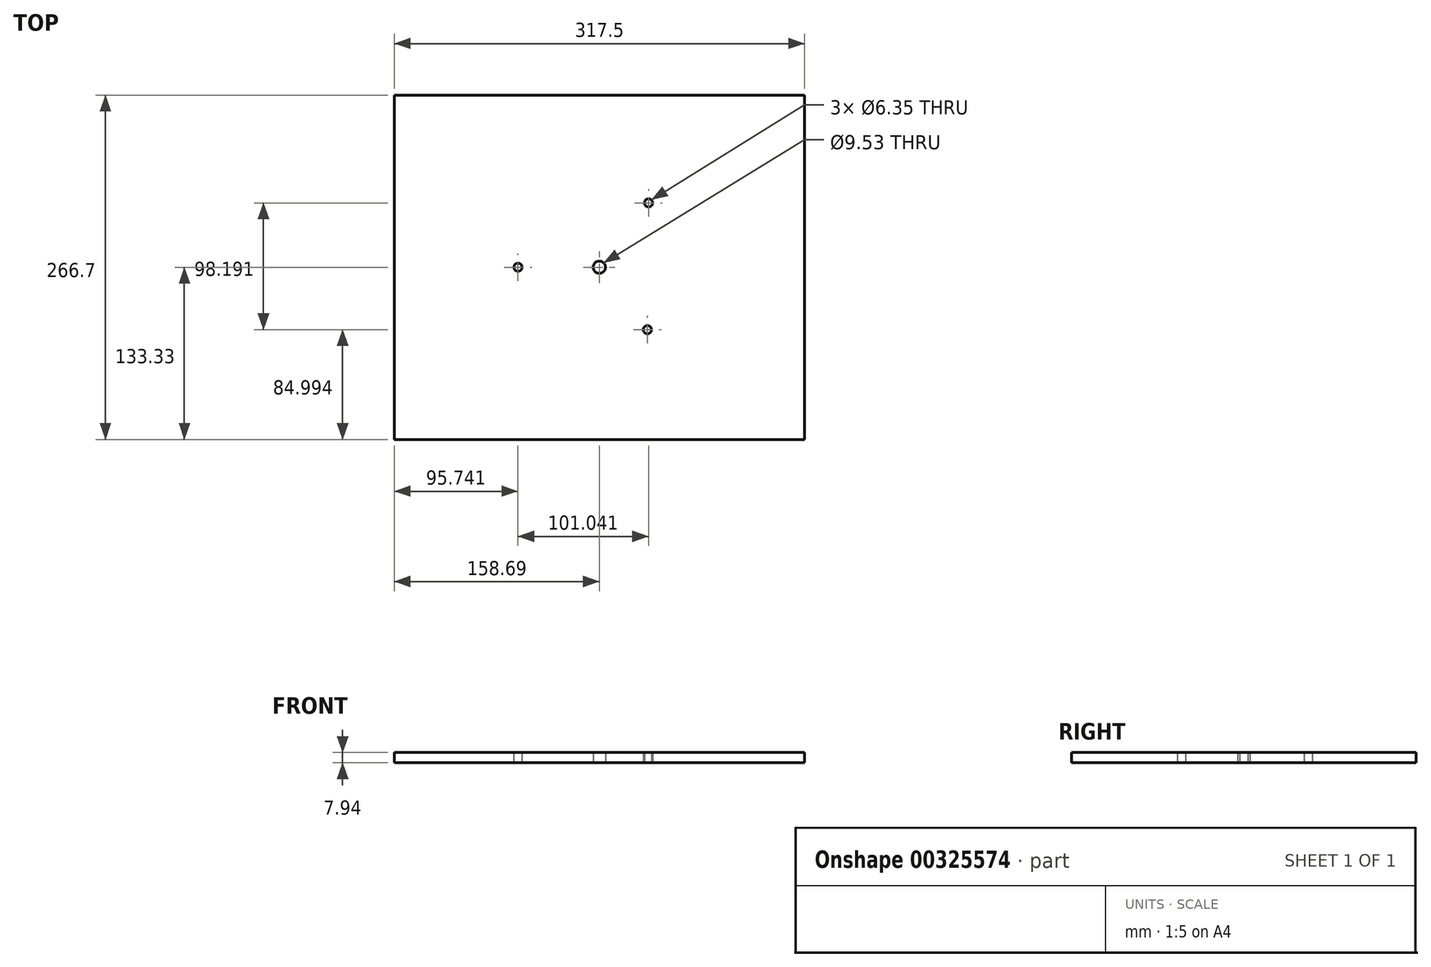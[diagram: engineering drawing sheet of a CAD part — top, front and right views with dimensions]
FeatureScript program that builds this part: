
annotation { "Feature Type Name" : "Feature", "Feature Type Description" : "" }
export const myFeature = defineFeature(function(context is Context, id is Id, definition is map)
    precondition{}
    {
        {
            var Q0;
            Q0=qCreatedBy(makeId("Top.planeOp"),FACE);
            var sketch = newSketch(context, id + "F0", { "sketchPlane" : qUnion([Q0])});
            skLineSegment(sketch, "E0.bottom", {"start": v(-158.69, 133.37) * mm, "end": v(158.81, 133.37) * mm});
            skLineSegment(sketch, "E0.top", {"start": v(-158.69, -133.33) * mm, "end": v(158.81, -133.33) * mm});
            skLineSegment(sketch, "E0.left", {"start": v(-158.69, 133.37) * mm, "end": v(-158.69, -133.33) * mm});
            skLineSegment(sketch, "E0.right", {"start": v(158.81, 133.37) * mm, "end": v(158.81, -133.33) * mm});
            skPoint(sketch, "E1", {"position": v(0.06, -133.33) * mm});
            skPoint(sketch, "E2", {"position": v(158.81, 0.02) * mm});
            skCircle(sketch, "E3", {"center": v(0, 0) * mm, "radius": 4.76 * mm});
            skCircle(sketch, "E4", {"center": v(-62.95, 0) * mm, "radius": 3.18 * mm});
            skCircle(sketch, "E5", {"center": v(38.1, 49.85) * mm, "radius": 3.18 * mm});
            skCircle(sketch, "E6", {"center": v(37.2, -48.34) * mm, "radius": 3.18 * mm});
            skSolve(sketch);
        }
        {
            var Q0;
            {var subQ1=sQuery(id+"F0.wireOp",EDGE,"E0.top");var subQ6=sQuery(id+"F0.wireOp",EDGE,"E0.left");var subQ9=makeQuery(id+"F0.imprint","INTERSECT",VERTEX,{"derivedFrom":[subQ1,subQ6]});Q0=makeQuery(id+"F0.imprint","IMPRINT",FACE,{"disambiguationData":[TD([[makeQuery(id+"F0.imprint","IMPRINT",EDGE,{"disambiguationData":[TD([[subQ9,-1.0]])],"derivedFrom":subQ1}),1.0]])]});}
            var Q1;
            {var subQ5=sQuery(id+"F0.wireOp",EDGE,"E0.top");var subQ7=sQuery(id+"F0.wireOp",EDGE,"JAwSw2JL-n3NN-2Vln-OLVn-L8GvoOgm2xYq");var subQ8=makeQuery(id+"F0.imprint","INTERSECT",VERTEX,{"derivedFrom":[subQ5,subQ7]});Q1=makeQuery(id+"F0.imprint","IMPRINT",FACE,{"disambiguationData":[TD([[makeQuery(id+"F0.imprint","IMPRINT",EDGE,{"disambiguationData":[TD([[subQ8,-1.0]])],"derivedFrom":subQ5}),1.0]])]});}
            var Q2;
            {var subQ1=sQuery(id+"F0.wireOp",EDGE,"E3");var subQ5=sQuery(id+"F0.wireOp",EDGE,"23pqLXLV-SrZZ-kslz-O0l0-19fHHKHyzlwI");var subQ6=makeQuery(id+"F0.imprint","INTERSECT",VERTEX,{"disambiguationData":[OD(1.0)],"derivedFrom":[subQ1,subQ5]});Q2=makeQuery(id+"F0.imprint","IMPRINT",FACE,{"disambiguationData":[TD([[makeQuery(id+"F0.imprint","IMPRINT",EDGE,{"disambiguationData":[TD([[subQ6,-1.0]])],"derivedFrom":subQ1}),-1.0]])]});}
            var Q3;
            {var subQ1=sQuery(id+"F0.wireOp",EDGE,"E0.left");var subQ5=sQuery(id+"F0.wireOp",EDGE,"23pqLXLV-SrZZ-kslz-O0l0-19fHHKHyzlwI");var subQ6=makeQuery(id+"F0.imprint","INTERSECT",VERTEX,{"derivedFrom":[subQ1,subQ5]});Q3=makeQuery(id+"F0.imprint","IMPRINT",FACE,{"disambiguationData":[TD([[makeQuery(id+"F0.imprint","IMPRINT",EDGE,{"disambiguationData":[TD([[subQ6,-1.0]])],"derivedFrom":subQ1}),1.0]])]});}
            var Q4;
            {var subQ1=sQuery(id+"F0.wireOp",EDGE,"E0.left");var subQ5=sQuery(id+"F0.wireOp",EDGE,"ks5EaK8h-8Zo1-6vaX-m6YF-OaYFmNDyZiSu");var subQ6=makeQuery(id+"F0.imprint","INTERSECT",VERTEX,{"derivedFrom":[subQ1,subQ5]});Q4=makeQuery(id+"F0.imprint","IMPRINT",FACE,{"disambiguationData":[TD([[makeQuery(id+"F0.imprint","IMPRINT",EDGE,{"disambiguationData":[TD([[subQ6,-1.0]])],"derivedFrom":subQ1}),1.0]])]});}
            var Q5;
            {var subQ0=sQuery(id+"F0.wireOp",EDGE,"OUGwM7Ne-J0Vz-JpQP-Of8x-XZFFkOnO35nF");var subQ1=sQuery(id+"F0.wireOp",EDGE,"E3");var subQ2=makeQuery(id+"F0.imprint","INTERSECT",VERTEX,{"disambiguationData":[OD(0.0)],"derivedFrom":[subQ1,subQ0]});Q5=makeQuery(id+"F0.imprint","IMPRINT",FACE,{"disambiguationData":[TD([[makeQuery(id+"F0.imprint","IMPRINT",EDGE,{"disambiguationData":[TD([[subQ2,-1.0]])],"derivedFrom":subQ1}),-1.0]])]});}
            var Q6;
            {var subQ1=sQuery(id+"F0.wireOp",EDGE,"E0.bottom");var subQ5=sQuery(id+"F0.wireOp",EDGE,"JAwSw2JL-n3NN-2Vln-OLVn-L8GvoOgm2xYq");var subQ6=makeQuery(id+"F0.imprint","INTERSECT",VERTEX,{"derivedFrom":[subQ1,subQ5]});Q6=makeQuery(id+"F0.imprint","IMPRINT",FACE,{"disambiguationData":[TD([[makeQuery(id+"F0.imprint","IMPRINT",EDGE,{"disambiguationData":[TD([[subQ6,-1.0]])],"derivedFrom":subQ1}),-1.0]])]});}
            var Q7;
            {var subQ1=sQuery(id+"F0.wireOp",EDGE,"E0.left");var subQ5=sQuery(id+"F0.wireOp",EDGE,"E0.bottom");var subQ6=makeQuery(id+"F0.imprint","INTERSECT",VERTEX,{"derivedFrom":[subQ5,subQ1]});Q7=makeQuery(id+"F0.imprint","IMPRINT",FACE,{"disambiguationData":[TD([[makeQuery(id+"F0.imprint","IMPRINT",EDGE,{"disambiguationData":[TD([[subQ6,-1.0]])],"derivedFrom":subQ5}),-1.0]])]});}
            var Q8;
            {var subQ1=sQuery(id+"F0.wireOp",EDGE,"E0.right");var subQ6=sQuery(id+"F0.wireOp",EDGE,"E0.bottom");var subQ9=makeQuery(id+"F0.imprint","INTERSECT",VERTEX,{"derivedFrom":[subQ6,subQ1]});Q8=makeQuery(id+"F0.imprint","IMPRINT",FACE,{"disambiguationData":[TD([[makeQuery(id+"F0.imprint","IMPRINT",EDGE,{"disambiguationData":[TD([[subQ9,1.0]])],"derivedFrom":subQ6}),-1.0]])]});}
            var Q9;
            {var subQ1=sQuery(id+"F0.wireOp",EDGE,"E0.bottom");var subQ5=sQuery(id+"F0.wireOp",EDGE,"OUGwM7Ne-J0Vz-JpQP-Of8x-XZFFkOnO35nF");var subQ6=makeQuery(id+"F0.imprint","INTERSECT",VERTEX,{"derivedFrom":[subQ1,subQ5]});Q9=makeQuery(id+"F0.imprint","IMPRINT",FACE,{"disambiguationData":[TD([[makeQuery(id+"F0.imprint","IMPRINT",EDGE,{"disambiguationData":[TD([[subQ6,-1.0]])],"derivedFrom":subQ1}),-1.0]])]});}
            var Q10;
            {var subQ7=sQuery(id+"F0.wireOp",EDGE,"OUGwM7Ne-J0Vz-JpQP-Of8x-XZFFkOnO35nF");var subQ8=sQuery(id+"F0.wireOp",EDGE,"E3");var subQ9=makeQuery(id+"F0.imprint","INTERSECT",VERTEX,{"disambiguationData":[OD(0.0)],"derivedFrom":[subQ8,subQ7]});Q10=makeQuery(id+"F0.imprint","IMPRINT",FACE,{"disambiguationData":[TD([[makeQuery(id+"F0.imprint","IMPRINT",EDGE,{"disambiguationData":[TD([[subQ9,1.0]])],"derivedFrom":subQ8}),-1.0]])]});}
            var Q11;
            {var subQ0=sQuery(id+"F0.wireOp",EDGE,"ks5EaK8h-8Zo1-6vaX-m6YF-OaYFmNDyZiSu");var subQ1=sQuery(id+"F0.wireOp",EDGE,"E0.right");var subQ2=makeQuery(id+"F0.imprint","INTERSECT",VERTEX,{"derivedFrom":[subQ1,subQ0]});Q11=makeQuery(id+"F0.imprint","IMPRINT",FACE,{"disambiguationData":[TD([[makeQuery(id+"F0.imprint","IMPRINT",EDGE,{"disambiguationData":[TD([[subQ2,-1.0]])],"derivedFrom":subQ1}),-1.0]])]});}
            var Q12;
            {var subQ0=sQuery(id+"F0.wireOp",EDGE,"23pqLXLV-SrZZ-kslz-O0l0-19fHHKHyzlwI");var subQ1=sQuery(id+"F0.wireOp",EDGE,"E3");var subQ2=makeQuery(id+"F0.imprint","INTERSECT",VERTEX,{"disambiguationData":[OD(0.0)],"derivedFrom":[subQ1,subQ0]});Q12=makeQuery(id+"F0.imprint","IMPRINT",FACE,{"disambiguationData":[TD([[makeQuery(id+"F0.imprint","IMPRINT",EDGE,{"disambiguationData":[TD([[subQ2,1.0]])],"derivedFrom":subQ1}),-1.0]])]});}
            var Q13;
            {var subQ0=sQuery(id+"F0.wireOp",EDGE,"23pqLXLV-SrZZ-kslz-O0l0-19fHHKHyzlwI");var subQ1=sQuery(id+"F0.wireOp",EDGE,"E0.right");var subQ2=makeQuery(id+"F0.imprint","INTERSECT",VERTEX,{"derivedFrom":[subQ1,subQ0]});Q13=makeQuery(id+"F0.imprint","IMPRINT",FACE,{"disambiguationData":[TD([[makeQuery(id+"F0.imprint","IMPRINT",EDGE,{"disambiguationData":[TD([[subQ2,-1.0]])],"derivedFrom":subQ1}),-1.0]])]});}
            var Q14;
            {var subQ1=sQuery(id+"F0.wireOp",EDGE,"OUGwM7Ne-J0Vz-JpQP-Of8x-XZFFkOnO35nF");var subQ5=sQuery(id+"F0.wireOp",EDGE,"E0.top");var subQ6=makeQuery(id+"F0.imprint","INTERSECT",VERTEX,{"derivedFrom":[subQ5,subQ1]});Q14=makeQuery(id+"F0.imprint","IMPRINT",FACE,{"disambiguationData":[TD([[makeQuery(id+"F0.imprint","IMPRINT",EDGE,{"disambiguationData":[TD([[subQ6,-1.0]])],"derivedFrom":subQ5}),1.0]])]});}
            var Q15;
            {var subQ1=sQuery(id+"F0.wireOp",EDGE,"E0.right");var subQ6=sQuery(id+"F0.wireOp",EDGE,"E0.top");var subQ9=makeQuery(id+"F0.imprint","INTERSECT",VERTEX,{"derivedFrom":[subQ6,subQ1]});Q15=makeQuery(id+"F0.imprint","IMPRINT",FACE,{"disambiguationData":[TD([[makeQuery(id+"F0.imprint","IMPRINT",EDGE,{"disambiguationData":[TD([[subQ9,1.0]])],"derivedFrom":subQ6}),1.0]])]});}
            extrude(context, id + "F1", {"entities" : qUnion([Q0, Q1, Q2, Q3, Q4, Q5, Q6, Q7, Q8, Q9, Q10, Q11, Q12, Q13, Q14, Q15]), "depth" : 7.94 * mm});
        }
    });
